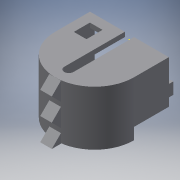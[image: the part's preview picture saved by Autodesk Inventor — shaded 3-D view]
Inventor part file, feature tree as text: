
AUTODESK INVENTOR PART (.ipt)
format: ipt  version: 2016 (Build 200138000, 138)  size: 255,488 bytes
history: native  units: in
note: dims shown in document units (in); Inventor stores cm internally (conversion verified against a paired STEP export)
features: sketch x13, extrude x12, reference x9, plane x1
ambient origin geometry x8: Origin, YZ Plane, XZ Plane, XY Plane, X Axis, Y Axis, Z Axis, Center Point
bodies: Solid1 (feature_tree)
feature tree (35):
  extrude  "Extrusion1"  Depth=1.5in TaperAngle=0.0deg
  extrude  "Extrusion2"  Depth=0.1969in TaperAngle=0.0deg
  extrude  "Extrusion3"  [1 undecoded]
  extrude  "Extrusion4"  Depth=0.3937in
  plane  "Work Plane1"
  sketch  "Sketch5"  dims[d12=1.9685in d14=0.9774in d15=0.3937in d17=1.0in d19=0.5in d20=0.0in]
  extrude  "Extrusion5"  Depth=0.3937in TaperAngle=0.0deg
  extrude  "Extrusion6"  Depth=100.0in TaperAngle=0.0deg
  extrude  "Extrusion7"  Depth=56.0in TaperAngle=0.0deg
  extrude  "Extrusion8"  Depth=0.3937in
  extrude  "Extrusion9"  Depth=1.0in TaperAngle=0.0deg
  extrude  "Extrusion10"  Depth=0.0787in
  extrude  "Extrusion11"  Depth=0.0787in
  extrude  "Extrusion12"  Depth=0.1in TaperAngle=0.0deg
  sketch  "Sketch1"  dims[d0=0.1969in d1=1.5in d2=0.0in]
  reference  "Reference1"
  sketch  "Sketch2"  dims[d3=4.6969in d4=0.0in d5=0.1969in d6=0.0in]
  sketch  "Sketch3"  dims[d7=0.1969in d8=0.0in d9=-1.697in]
  sketch  "Sketch4"  dims[d10=0.7874in d11=0.3937in]
  reference  "Reference2"
  sketch  "Sketch6"  dims[d21=0.197in d22=0.0in d23=100.0in d24=0.0in]
  sketch  "Sketch8"  dims[d25=0.5in d26=56.0in d27=0.0in]
  reference  "Reference3"
  reference  "Reference4"
  reference  "Reference5"
  reference  "Reference6"
  sketch  "Sketch9"  dims[d28=0.3937in d29=0.3937in]
  sketch  "Sketch10"  dims[d30=56.0in d31=0.0in d32=1.0in d33=0.0in]
  sketch  "Sketch11"  dims[d34=0.0787in d35=0.0787in]
  sketch  "Sketch12"  dims[d36=0.0787in d37=0.0787in]
  sketch  "Sketch13"  dims[d38=1.0in d39=0.0in d40=0.1in d41=0.0in]
  reference  "Reference7"
  sketch  "Sketch14"
  reference  "Reference8"
  reference  "Reference9"
note: 1 required parameter value undecoded (feature->parameter linkage not recoverable at this tier; creation-order binding heuristic only, values carry confidence <= 0.55)
